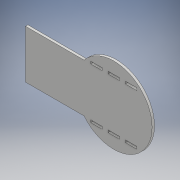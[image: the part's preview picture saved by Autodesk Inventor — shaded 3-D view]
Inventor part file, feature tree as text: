
AUTODESK INVENTOR PART (.ipt)
format: ipt  version: 2018 (Build 220112000, 112)  size: 144,384 bytes
history: native  units: mm
features: extrude x5, sketch x5, other x1
ambient origin geometry x8: Origin, YZ Plane, XZ Plane, XY Plane, X Axis, Y Axis, Z Axis, Center Point
bodies: Body1 (feature_tree)
feature tree (11):
  other  "Sólido1"
  extrude  "Extrusión1"  Depth=3.0mm
  extrude  "Extrusión2"  Depth=10.0mm
  extrude  "Extrusión3"  Depth=3.0mm TaperAngle=0.0deg
  extrude  "Extrusión4"  [1 undecoded]
  extrude  "Extrusión5"  [1 undecoded]
  sketch  "Boceto1"  dims[d19=3.0mm d20=0.0mm d23=7.0mm]
  sketch  "Boceto2"  dims[d24=10.0mm d25=0.0mm d26=9.0mm]
  sketch  "Boceto3"  dims[d27=10.0mm d28=0.0mm d32=3.0mm d33=0.0mm]
  sketch  "Boceto4"  dims[d34=3.0mm d35=0.0mm]
  sketch  "Boceto5"
note: 2 required parameter values undecoded (feature->parameter linkage not recoverable at this tier; creation-order binding heuristic only, values carry confidence <= 0.55)
